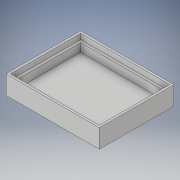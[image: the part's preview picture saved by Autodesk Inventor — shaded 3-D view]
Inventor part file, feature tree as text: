
AUTODESK INVENTOR PART (.ipt)
format: ipt  version: 2019 (Build 230136000, 136)  size: 123,392 bytes
history: native  units: mm
features: extrude x3, sketch x3, projected_geometry x2
ambient origin geometry x8: Origin, YZ Plane, XZ Plane, XY Plane, X Axis, Y Axis, Z Axis, Center Point
bodies: Volumenkörper1 (feature_tree)
feature tree (8):
  extrude  "Extrusion1"  Depth=80.0mm
  extrude  "Extrusion2"  Depth=90.0mm
  extrude  "Extrusion3"  Depth=15.0mm TaperAngle=0.0deg
  sketch  "Skizze1"  dims[d0=100.0mm d1=80.0mm]
  sketch  "Skizze2"  dims[d2=5.0mm d3=0.0mm d4=90.0mm]
  projected_geometry  "Projizierte Kontur1"
  sketch  "Skizze3"  dims[d5=70.0mm d6=15.0mm d7=0.0mm d8=95.5mm d9=75.5mm d10=6.0mm d11=0.0mm]
  projected_geometry  "Projizierte Kontur2"
